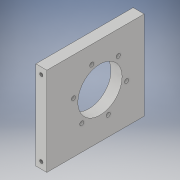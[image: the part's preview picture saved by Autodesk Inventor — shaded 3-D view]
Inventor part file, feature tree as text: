
AUTODESK INVENTOR PART (.ipt)
format: ipt  version: 2019 (Build 230136000, 136)  size: 146,432 bytes
history: native  units: in
note: dims shown in document units (in); Inventor stores cm internally (conversion verified against a paired STEP export)
features: sketch x4, hole x3, projected_geometry x2, extrude x1
ambient origin geometry x8: Origin, YZ Plane, XZ Plane, XY Plane, X Axis, Y Axis, Z Axis, Center Point
bodies: Solid1 (feature_tree)
feature tree (10):
  extrude  "Extrusion1"  Depth=2.2in
  hole  "Hole1"  [1 undecoded]
  hole  "Hole2"  [1 undecoded]
  hole  "Hole4"  [1 undecoded]
  sketch  "Sketch1"  dims[d0=1.0in d1=2.2in]
  sketch  "Sketch2"  dims[d4=1.0in d5=0.98in]
  projected_geometry  "Projected Loop1"
  sketch  "Sketch3"  dims[d6=2.0in d7=0.25in d8=0.0in]
  sketch  "Sketch5"  dims[d9=0.25in d10=0.125in d11=0.125in d12=0.15in d13=0.15in d14=0.076in d15=0.198in d16=0.119in d17=0.25in d18=0.5635in d19=0.302in d20=0.8108in d21=0.613in d22=2.3622in d24=360.0deg d26=0.092in d27=0.198in d28=0.119in d29=0.25in d30=0.5635in d31=0.302in d32=0.8108in d42=0.25in d43=0.25in d44=0.076in d45=0.198in d46=0.375in d47=0.25in d48=0.5635in d49=0.302in d50=0.8108in]
  projected_geometry  "Projected Loop3"
note: 3 required parameter values undecoded (feature->parameter linkage not recoverable at this tier; creation-order binding heuristic only, values carry confidence <= 0.55)
